# Revit family: Sanitary_Wash-Basins_hansgrohe_50120CHN-MellowTide-Waste-set-non-closin
name_source: partatom
category: Plumbing Fixtures
revit_build: Autodesk Revit 2018 (Build: 20190510_1515(x64)
units: mm (PartAtom-declared; Revit-internal decimal feet)

## family parameters
Always vertical = No
Cut with Voids When Loaded = No
OmniClass Number = 23.27.31.00
OmniClass Title = Valves
Part Type = Normal
Room Calculation Point = No
Round Connector Dimension = Use Diameter
Shared = No
Work Plane-Based = Yes

## types (1)
- 007 White
    Always visible = Yes
    BIMobject category = Wash Basins
    Default Elevation = 1219.2 mm  [stored 4 ft]
    Description = MellowTide Waste set non-closing for washbasins with ceramic cover
    Design country = Germany
    EAN code = 4059625401675
    Edition number = 1
    GTIN code = https://4059625401675
    IFC Classification = Sanitary Terminal
    Installation instructions = https://www.hansgrohe.com
    Manufacturer = Hansgrohe
    Manufacturer country = Germany
    Manufacturer name = hansgrohe
    Material = Hansgrohe - Ceramic - 007 White
    Model = 50120CHN
    Product Guid = 6ba2ce15-acdd-4a37-adb5-2bbc823de040
    Product SKU = 50120CHN
    Product data url = https://bimobject.com
    Product family = MellowTide
    Product group = Waste systems washbasin
    Product name = 50120CHN MellowTide Waste set non-closing for washbasins with ceramic cover
    Product url = https://www.hansgrohe.com
    QR code = https://bimobject.com
    URL = https://www.hansgrohe.com
    Weight Net (Kg) = 389

note: [stored X ft] marks values corroborated as IEEE doubles in the binary element streams (Revit-internal decimal feet)

## geometry (parser evidence)
native form markers: Sweep x3
no freeform markers — native parametric forms only
